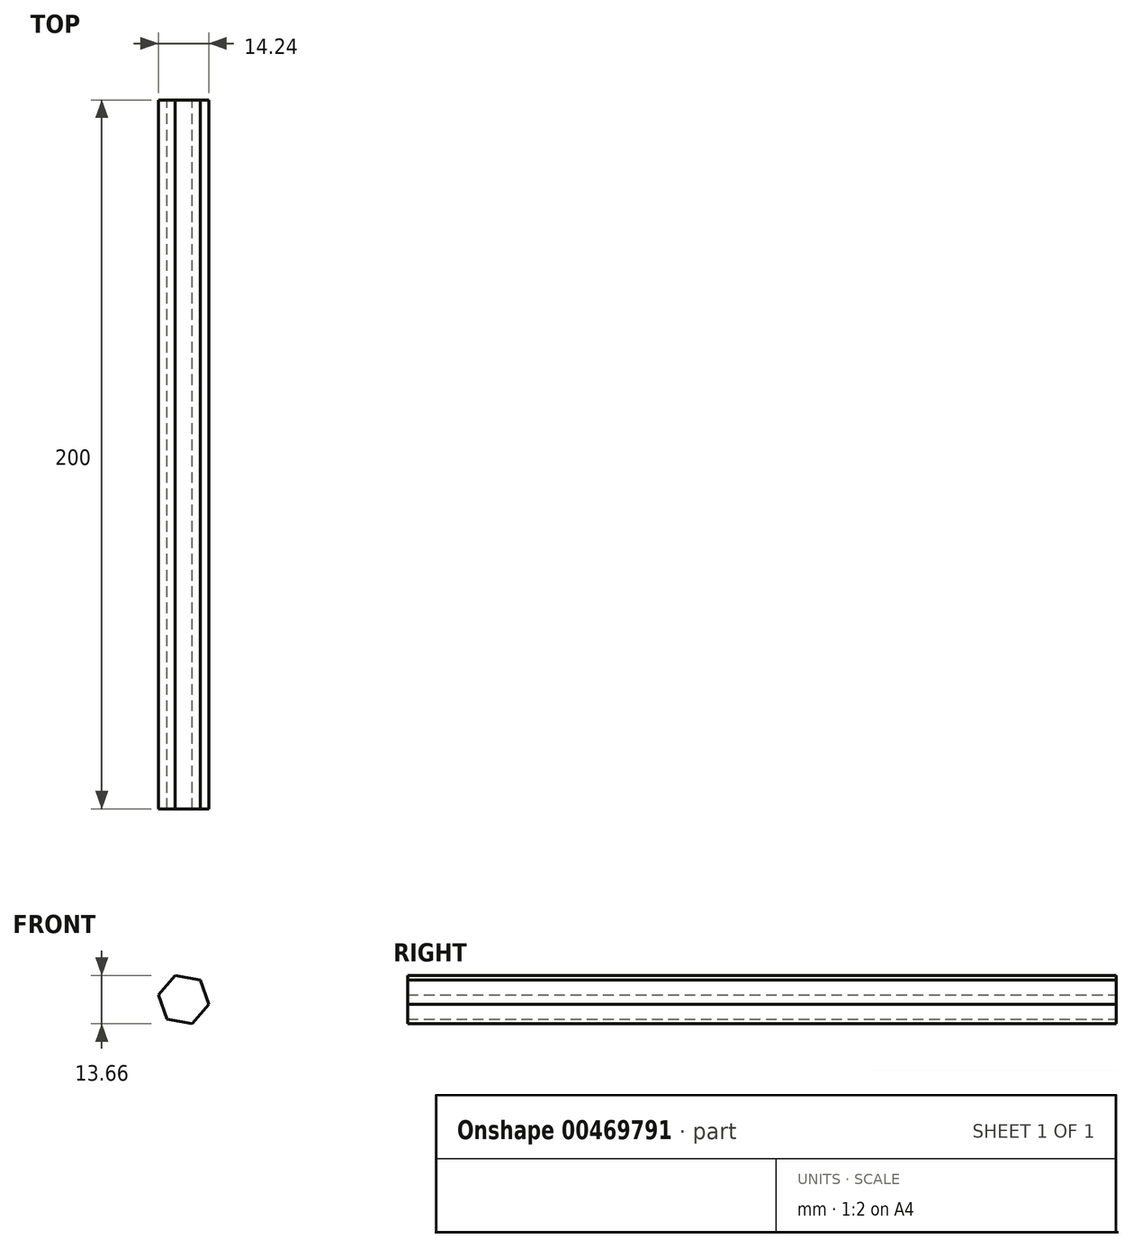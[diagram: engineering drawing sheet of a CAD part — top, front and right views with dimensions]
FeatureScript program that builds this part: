
annotation { "Feature Type Name" : "Feature", "Feature Type Description" : "" }
export const myFeature = defineFeature(function(context is Context, id is Id, definition is map)
    precondition{}
    {
        {
            var Q0;
            Q0=qCreatedBy(makeId("Front.planeOp"),FACE);
            var sketch = newSketch(context, id + "F0", { "sketchPlane" : qUnion([Q0])});
            skCircle(sketch, "E0.cCircle", {"center": v(0, 0) * mm, "radius": 7.24 * mm, "construction": true});
            skLineSegment(sketch, "E0.0", {"start": v(4.71, 5.5) * mm, "end": v(7.12, -1.33) * mm});
            skLineSegment(sketch, "E0.1", {"start": v(7.12, -1.33) * mm, "end": v(2.4, -6.83) * mm});
            skLineSegment(sketch, "E0.2", {"start": v(2.4, -6.83) * mm, "end": v(-4.71, -5.5) * mm});
            skLineSegment(sketch, "E0.3", {"start": v(-4.71, -5.5) * mm, "end": v(-7.12, 1.33) * mm});
            skLineSegment(sketch, "E0.4", {"start": v(-7.12, 1.33) * mm, "end": v(-2.4, 6.83) * mm});
            skLineSegment(sketch, "E0.5", {"start": v(-2.4, 6.83) * mm, "end": v(4.71, 5.5) * mm});
            skLineSegment(sketch, "E1", {"start": v(0, 0) * mm, "end": v(4.71, 5.5) * mm});
            skSolve(sketch);
        }
        {
            var Q0;
            Q0=makeQuery(id+"F0.imprint","IMPRINT",FACE,{"disambiguationData":[TD([[makeQuery(id+"F0.imprint","IMPRINT",EDGE,{"derivedFrom":sQuery(id+"F0.wireOp",EDGE,"E0.0")}),-1.0]])]});
            extrude(context, id + "F1", {"entities" : qUnion([Q0]), "depth" : 200 * mm});
        }
    });
